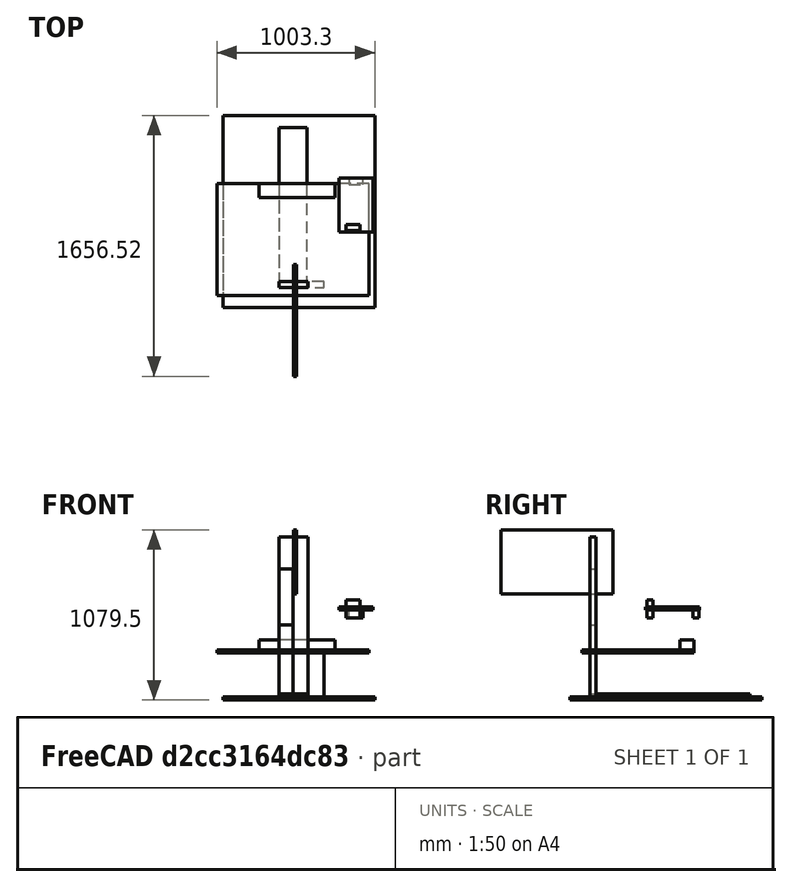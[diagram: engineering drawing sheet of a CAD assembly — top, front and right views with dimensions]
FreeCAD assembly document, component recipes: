
FREECAD ASSEMBLY — COMPONENT RECIPES ("flightDeck-rough")

This assembly document has 22 components, labeled P0..P21 below (a component is one placed body or linked part). 22 of them carry a construction recipe — the FreeCAD feature program that regenerates the part from scratch, quoted from this document or its linked companion documents; the rest are supplied as boundary geometry only. No exploded tour is included for this assembly.
COMPONENT P0 — recipe-attached ("panel-chairDeck", modeled in this document).
Construction recipe (the document's own serialized feature program — sketch geometry with constraints, then the solid features built on it; lengths are millimeters unless a unit is written):

FEATURE [Sketcher::SketchObject] Sketch013
  ArcFitTolerance = 1e-06
  AttachmentSupport = -> [XY_Plane007]
  ExternalBSplineMaxDegree = 5
  ExternalBSplineTolerance = 0.0001
  FixShape = 1
  FullyConstrained = true
  InternalTolerance = 1e-06
  InvalidShape = false
  MakeInternals = false
  MapMode = 5
  Support = -> [XY_Plane007]
  TreeRank = 114
  ValidateShape = false
  sketch-geometry (4):
    g0: LineSegment StartX=0 StartY=0 StartZ=0 EndX=965.2 EndY=0 EndZ=0
    g1: LineSegment StartX=965.2 StartY=0 StartZ=0 EndX=965.2 EndY=711.2 EndZ=0
    g2: LineSegment StartX=965.2 StartY=711.2 StartZ=0 EndX=0 EndY=711.2 EndZ=0
    g3: LineSegment StartX=0 StartY=711.2 StartZ=0 EndX=0 EndY=0 EndZ=0
  constraints (11):
    c: Coincident(g0,g1)
    c: Coincident(g1,g2)
    c: Coincident(g2,g3)
    c: Coincident(g3,g0)
    c: Horizontal(g0)
    c: Horizontal(g2)
    c: Vertical(g1)
    c: Vertical(g3)
    c: Coincident(g0,g-1)
    c: DistanceX(g0,g0) = 965.2
    c: DistanceY(g3,g3) = 711.2
FEATURE [PartDesign::Pad] Pad001
  AddSubType = 0
  AlongSketchNormal = false
  AutoTaperInnerAngle = true
  CheckUpToFaceLimits = true
  ClaimChildren = false
  Direction = (0,0,1)
  Fit = 0
  FitJoin = 0
  FixShape = 1
  InnerFit = 0
  InnerFitJoin = 0
  InvalidShape = false
  Length = 19.05
  Length2 = 100
  Linearize = true
  NewSolid = false
  Profile = -> Sketch013
  Refine = true
  Suppress = false
  TaperInnerAngle = 0
  TaperInnerAngleRev = 0
  TreeRank = 115
  Type = 0
  ValidateShape = false
  _ProfileBasedVersion = 1
FEATURE [PartDesign::Body] Body007  label="panel-chairDeck"
  AutoGroupSolids = false
  ClaimAllChildren = false
  ExportMode = 0
  FixShape = 1
  Group = -> [Sketch013,Pad001]
  InvalidShape = false
  Origin = -> Origin007
  Placement = pos=(-393.7,-50.7998,279.4) rot=(0,0,1;0rad)
  Tip = -> Pad001
  TreeRank = 113
  ValidateShape = false
  _ExportChildren = -> [Pad001]
  _GroupVersion = 1
COMPONENT P1 — recipe-attached ("panel-chairFloor", modeled in this document).
Construction recipe (the document's own serialized feature program — sketch geometry with constraints, then the solid features built on it; lengths are millimeters unless a unit is written):

FEATURE [Sketcher::SketchObject] Sketch014
  ArcFitTolerance = 1e-06
  AttachmentSupport = -> [XY_Plane008]
  ExternalBSplineMaxDegree = 5
  ExternalBSplineTolerance = 0.0001
  FixShape = 1
  FullyConstrained = true
  InternalTolerance = 1e-06
  InvalidShape = false
  MakeInternals = false
  MapMode = 5
  Support = -> [XY_Plane008]
  TreeRank = 126
  ValidateShape = false
  sketch-geometry (4):
    g0: LineSegment StartX=0 StartY=0 StartZ=0 EndX=965.2 EndY=0 EndZ=0
    g1: LineSegment StartX=965.2 StartY=0 StartZ=0 EndX=965.2 EndY=1219.2 EndZ=0
    g2: LineSegment StartX=965.2 StartY=1219.2 StartZ=0 EndX=0 EndY=1219.2 EndZ=0
    g3: LineSegment StartX=0 StartY=1219.2 StartZ=0 EndX=0 EndY=0 EndZ=0
  constraints (11):
    c: Coincident(g0,g1)
    c: Coincident(g1,g2)
    c: Coincident(g2,g3)
    c: Coincident(g3,g0)
    c: Horizontal(g0)
    c: Horizontal(g2)
    c: Vertical(g1)
    c: Vertical(g3)
    c: Coincident(g0,g-1)
    c: DistanceX(g0,g0) = 965.2
    c: DistanceY(g3,g3) = 1219.2
FEATURE [PartDesign::Pad] Pad002
  AddSubType = 0
  AlongSketchNormal = false
  AutoTaperInnerAngle = true
  CheckUpToFaceLimits = true
  ClaimChildren = false
  Direction = (0,0,1)
  Fit = 0
  FitJoin = 0
  FixShape = 1
  InnerFit = 0
  InnerFitJoin = 0
  InvalidShape = false
  Length = 19.05
  Length2 = 100
  Linearize = true
  NewSolid = false
  Profile = -> Sketch014
  Refine = true
  Suppress = false
  TaperInnerAngle = 0
  TaperInnerAngleRev = 0
  TreeRank = 127
  Type = 0
  ValidateShape = false
  _ProfileBasedVersion = 1
FEATURE [PartDesign::Body] Body008  label="panel-chairFloor"
  AutoGroupSolids = false
  ClaimAllChildren = false
  ExportMode = 0
  FixShape = 1
  Group = -> [Sketch014,Pad002]
  InvalidShape = false
  Origin = -> Origin008
  Placement = pos=(-355.6,-127,-19.0502) rot=(0,0,1;0rad)
  Tip = -> Pad002
  TreeRank = 125
  ValidateShape = false
  _ExportChildren = -> [Pad002]
  _GroupVersion = 1
COMPONENT P2 — recipe-attached ("panel-pedalsDeck", modeled in this document).
Construction recipe (the document's own serialized feature program — sketch geometry with constraints, then the solid features built on it; lengths are millimeters unless a unit is written):

FEATURE [Sketcher::SketchObject] Sketch016
  ArcFitTolerance = 1e-06
  AttachmentSupport = -> [XY_Plane010]
  ExternalBSplineMaxDegree = 5
  ExternalBSplineTolerance = 0.0001
  FixShape = 1
  FullyConstrained = false
  InternalTolerance = 1e-06
  InvalidShape = false
  MakeInternals = false
  MapMode = 5
  Support = -> [XY_Plane010]
  TreeRank = 159
  ValidateShape = false
  sketch-geometry (4):
    g0: LineSegment StartX=-351.816 StartY=864.428 StartZ=0 EndX=359.384 EndY=864.428 EndZ=0
    g1: LineSegment StartX=359.384 StartY=864.428 StartZ=0 EndX=359.384 EndY=1270.83 EndZ=0
    g2: LineSegment StartX=359.384 StartY=1270.83 StartZ=0 EndX=-351.816 EndY=1270.83 EndZ=0
    g3: LineSegment StartX=-351.816 StartY=1270.83 StartZ=0 EndX=-351.816 EndY=864.428 EndZ=0
  constraints (10):
    c: Coincident(g0,g1)
    c: Coincident(g1,g2)
    c: Coincident(g2,g3)
    c: Coincident(g3,g0)
    c: Horizontal(g0)
    c: Horizontal(g2)
    c: Vertical(g1)
    c: Vertical(g3)
    c: DistanceX(g0,g0) = 711.2
    c: DistanceY(g1,g1) = 406.4
FEATURE [PartDesign::Pad] Pad004
  AddSubType = 0
  AlongSketchNormal = false
  AutoTaperInnerAngle = true
  CheckUpToFaceLimits = true
  ClaimChildren = false
  Direction = (0,0,1)
  Fit = 0
  FitJoin = 0
  FixShape = 1
  InnerFit = 0
  InnerFitJoin = 0
  InvalidShape = false
  Length = 19.05
  Length2 = 100
  Linearize = true
  NewSolid = false
  Profile = -> Sketch016
  Refine = true
  Suppress = false
  TaperInnerAngle = 0
  TaperInnerAngleRev = 0
  TreeRank = 160
  Type = 0
  ValidateShape = false
  _ProfileBasedVersion = 1
FEATURE [PartDesign::Body] Body010  label="panel-pedalsDeck"
  AutoGroupSolids = false
  ClaimAllChildren = false
  ExportMode = 0
  FixShape = 1
  Group = -> [Sketch016,Pad004]
  InvalidShape = false
  Origin = -> Origin010
  Placement = pos=(92.6838,-212.506,-210.378) rot=(0.57735,0.57735,0.57735;2.0944rad)
  Tip = -> Pad004
  TreeRank = 158
  ValidateShape = false
  _ExportChildren = -> [Pad004]
  _GroupVersion = 1
COMPONENT P3 — recipe-attached ("timber-tilt", modeled in this document).
Construction recipe (the document's own serialized feature program — sketch geometry with constraints, then the solid features built on it; lengths are millimeters unless a unit is written):

FEATURE [Sketcher::SketchObject] Sketch018
  ArcFitTolerance = 1e-06
  AttachmentSupport = -> [XY_Plane012]
  ExternalBSplineMaxDegree = 5
  ExternalBSplineTolerance = 0.0001
  FixShape = 1
  FullyConstrained = true
  InternalTolerance = 1e-06
  InvalidShape = false
  MakeInternals = false
  MapMode = 5
  Support = -> [XY_Plane012]
  TreeRank = 191
  ValidateShape = false
  sketch-geometry (4):
    g0: LineSegment StartX=0 StartY=0 StartZ=0 EndX=88.9 EndY=0 EndZ=0
    g1: LineSegment StartX=88.9 StartY=0 StartZ=0 EndX=88.9 EndY=63.5 EndZ=0
    g2: LineSegment StartX=88.9 StartY=63.5 StartZ=0 EndX=0 EndY=63.5 EndZ=0
    g3: LineSegment StartX=0 StartY=63.5 StartZ=0 EndX=0 EndY=0 EndZ=0
  constraints (11):
    c: Coincident(g0,g1)
    c: Coincident(g1,g2)
    c: Coincident(g2,g3)
    c: Coincident(g3,g0)
    c: Horizontal(g0)
    c: Horizontal(g2)
    c: Vertical(g1)
    c: Vertical(g3)
    c: Coincident(g0,g-1)
    c: DistanceX(g0,g0) = 88.9
    c: DistanceY(g3,g3) = 63.5
FEATURE [PartDesign::Pad] Pad006
  AddSubType = 0
  AlongSketchNormal = false
  AutoTaperInnerAngle = true
  CheckUpToFaceLimits = true
  ClaimChildren = false
  Direction = (0,0,1)
  Fit = 0
  FitJoin = 0
  FixShape = 1
  InnerFit = 0
  InnerFitJoin = 0
  InvalidShape = false
  Length = 482.6
  Length2 = 100
  Linearize = true
  NewSolid = false
  Profile = -> Sketch018
  Refine = true
  Suppress = false
  TaperInnerAngle = 0
  TaperInnerAngleRev = 0
  TreeRank = 192
  Type = 0
  ValidateShape = false
  _ProfileBasedVersion = 1
FEATURE [PartDesign::Body] Body012  label="timber-tilt"
  AutoGroupSolids = false
  ClaimAllChildren = false
  ExportMode = 0
  FixShape = 1
  Group = -> [Sketch018,Pad006]
  InvalidShape = false
  Origin = -> Origin012
  Placement = pos=(355.6,660.4,298.45) rot=(0.57735,-0.57735,-0.57735;2.0944rad)
  Tip = -> Pad006
  TreeRank = 190
  ValidateShape = false
  _ExportChildren = -> [Pad006]
  _GroupVersion = 1
COMPONENT P4 — recipe-attached ("timber-sideStick", modeled in this document).
Construction recipe (the document's own serialized feature program — sketch geometry with constraints, then the solid features built on it; lengths are millimeters unless a unit is written):

FEATURE [Sketcher::SketchObject] Sketch022
  ArcFitTolerance = 1e-06
  AttachmentSupport = -> [XY_Plane016]
  ExternalBSplineMaxDegree = 5
  ExternalBSplineTolerance = 0.0001
  FixShape = 1
  FullyConstrained = true
  InternalTolerance = 1e-06
  InvalidShape = false
  MakeInternals = false
  MapMode = 5
  Support = -> [XY_Plane016]
  TreeRank = 244
  ValidateShape = false
  sketch-geometry (4):
    g0: LineSegment StartX=0 StartY=0 StartZ=0 EndX=88.9 EndY=0 EndZ=0
    g1: LineSegment StartX=88.9 StartY=0 StartZ=0 EndX=88.9 EndY=38.1 EndZ=0
    g2: LineSegment StartX=88.9 StartY=38.1 StartZ=0 EndX=0 EndY=38.1 EndZ=0
    g3: LineSegment StartX=0 StartY=38.1 StartZ=0 EndX=0 EndY=0 EndZ=0
  constraints (11):
    c: Coincident(g0,g1)
    c: Coincident(g1,g2)
    c: Coincident(g2,g3)
    c: Coincident(g3,g0)
    c: Horizontal(g0)
    c: Horizontal(g2)
    c: Vertical(g1)
    c: Vertical(g3)
    c: Coincident(g0,g-1)
    c: DistanceY(g3,g3) = 38.1
    c: DistanceX(g0,g0) = 88.9
FEATURE [PartDesign::Pad] Pad010
  AddSubType = 0
  AlongSketchNormal = false
  AutoTaperInnerAngle = true
  CheckUpToFaceLimits = true
  ClaimChildren = false
  Direction = (0,0,1)
  Fit = 0
  FitJoin = 0
  FixShape = 1
  InnerFit = 0
  InnerFitJoin = 0
  InvalidShape = false
  Length = 114.3
  Length2 = 100
  Linearize = true
  NewSolid = false
  Profile = -> Sketch022
  Refine = true
  Suppress = false
  TaperInnerAngle = 0
  TaperInnerAngleRev = 0
  TreeRank = 245
  Type = 0
  ValidateShape = false
  _ProfileBasedVersion = 1
FEATURE [PartDesign::Body] Body016  label="timber-sideStick"
  AutoGroupSolids = false
  ClaimAllChildren = false
  ExportMode = 0
  FixShape = 1
  Group = -> [Sketch022,Pad010]
  InvalidShape = false
  Origin = -> Origin016
  Placement = pos=(425.45,361.95,501.65) rot=(0,0,1;0rad)
  Tip = -> Pad010
  TreeRank = 247
  ValidateShape = false
  _ExportChildren = -> [Pad010]
  _GroupVersion = 1
COMPONENT P5 — recipe-attached ("timber-sideStick-front", modeled in this document).
Construction recipe (the document's own serialized feature program — sketch geometry with constraints, then the solid features built on it; lengths are millimeters unless a unit is written):

FEATURE [Sketcher::SketchObject] Sketch023
  ArcFitTolerance = 1e-06
  AttachmentSupport = -> [XY_Plane017]
  ExternalBSplineMaxDegree = 5
  ExternalBSplineTolerance = 0.0001
  FixShape = 1
  FullyConstrained = true
  InternalTolerance = 1e-06
  InvalidShape = false
  MakeInternals = false
  MapMode = 5
  Support = -> [XY_Plane017]
  TreeRank = 259
  ValidateShape = false
  sketch-geometry (4):
    g0: LineSegment StartX=0 StartY=0 StartZ=0 EndX=88.9 EndY=0 EndZ=0
    g1: LineSegment StartX=88.9 StartY=0 StartZ=0 EndX=88.9 EndY=38.1 EndZ=0
    g2: LineSegment StartX=88.9 StartY=38.1 StartZ=0 EndX=0 EndY=38.1 EndZ=0
    g3: LineSegment StartX=0 StartY=38.1 StartZ=0 EndX=0 EndY=0 EndZ=0
  constraints (11):
    c: Coincident(g0,g1)
    c: Coincident(g1,g2)
    c: Coincident(g2,g3)
    c: Coincident(g3,g0)
    c: Horizontal(g0)
    c: Horizontal(g2)
    c: Vertical(g1)
    c: Vertical(g3)
    c: Coincident(g0,g-1)
    c: DistanceY(g3,g3) = 38.1
    c: DistanceX(g0,g0) = 88.9
FEATURE [PartDesign::Pad] Pad011
  AddSubType = 0
  AlongSketchNormal = false
  AutoTaperInnerAngle = true
  CheckUpToFaceLimits = true
  ClaimChildren = false
  Direction = (0,0,1)
  Fit = 0
  FitJoin = 0
  FixShape = 1
  InnerFit = 0
  InnerFitJoin = 0
  InvalidShape = false
  Length = 69.85
  Length2 = 100
  Linearize = true
  NewSolid = false
  Profile = -> Sketch023
  Refine = true
  Suppress = false
  TaperInnerAngle = 0
  TaperInnerAngleRev = 0
  TreeRank = 260
  Type = 0
  ValidateShape = false
  _ProfileBasedVersion = 1
FEATURE [PartDesign::Body] Body017  label="timber-sideStick-front"
  AutoGroupSolids = false
  ClaimAllChildren = false
  ExportMode = 0
  FixShape = 1
  Group = -> [Sketch023,Pad011]
  InvalidShape = false
  Origin = -> Origin017
  Placement = pos=(444.5,654.05,501.65) rot=(0,0,1;0rad)
  Tip = -> Pad011
  TreeRank = 258
  ValidateShape = false
  _ExportChildren = -> [Pad011]
  _GroupVersion = 1
COMPONENT P6 — recipe-attached ("Link(timber-floorToChair)", modeled in this document).
Construction recipe (the document's own serialized feature program — sketch geometry with constraints, then the solid features built on it; lengths are millimeters unless a unit is written):

FEATURE [Sketcher::SketchObject] Sketch012
  ArcFitTolerance = 1e-06
  AttachmentSupport = -> [XY_Plane006]
  ExternalBSplineMaxDegree = 5
  ExternalBSplineTolerance = 0.0001
  FixShape = 1
  FullyConstrained = true
  InternalTolerance = 1e-06
  InvalidShape = false
  MakeInternals = false
  MapMode = 5
  Support = -> [XY_Plane006]
  TreeRank = 92
  ValidateShape = false
  sketch-geometry (4):
    g0: LineSegment StartX=0 StartY=0 StartZ=0 EndX=285.75 EndY=0 EndZ=0
    g1: LineSegment StartX=285.75 StartY=0 StartZ=0 EndX=285.75 EndY=38.1 EndZ=0
    g2: LineSegment StartX=285.75 StartY=38.1 StartZ=0 EndX=0 EndY=38.1 EndZ=0
    g3: LineSegment StartX=0 StartY=38.1 StartZ=0 EndX=0 EndY=0 EndZ=0
  constraints (11):
    c: Coincident(g0,g1)
    c: Coincident(g1,g2)
    c: Coincident(g2,g3)
    c: Coincident(g3,g0)
    c: Horizontal(g0)
    c: Horizontal(g2)
    c: Vertical(g1)
    c: Vertical(g3)
    c: Coincident(g0,g-1)
    c: DistanceX(g0,g0) = 285.75
    c: DistanceY(g3,g3) = 38.1
FEATURE [PartDesign::Pad] Pad
  AddSubType = 0
  AlongSketchNormal = false
  AutoTaperInnerAngle = true
  CheckUpToFaceLimits = true
  ClaimChildren = false
  Direction = (0,0,1)
  Fit = 0
  FitJoin = 0
  FixShape = 1
  InnerFit = 0
  InnerFitJoin = 0
  InvalidShape = false
  Length = 279.4
  Length2 = 100
  Linearize = true
  NewSolid = false
  Profile = -> Sketch012
  Refine = true
  Suppress = false
  TaperInnerAngle = 0
  TaperInnerAngleRev = 0
  TreeRank = 93
  Type = 0
  ValidateShape = false
  _ProfileBasedVersion = 1
FEATURE [PartDesign::Body] Body006  label="timber-floorToChair"
  AutoGroupSolids = false
  ClaimAllChildren = false
  ExportMode = 0
  FixShape = 1
  Group = -> [Sketch012,Pad]
  InvalidShape = false
  Origin = -> Origin006
  Tip = -> Pad
  TreeRank = 94
  ValidateShape = false
  _ExportChildren = -> [Pad]
  _GroupVersion = 1
COMPONENT P7 — same part as P6; its construction recipe is shown at P6.
COMPONENT P8 — same part as P6; its construction recipe is shown at P6.
COMPONENT P9 — same part as P6; its construction recipe is shown at P6.
COMPONENT P10 — same part as P6; its construction recipe is shown at P6.
COMPONENT P11 — same part as P6; its construction recipe is shown at P6.
COMPONENT P12 — recipe-attached ("Link006(timber-floorToPedals)", modeled in this document).
Construction recipe (the document's own serialized feature program — sketch geometry with constraints, then the solid features built on it; lengths are millimeters unless a unit is written):

FEATURE [Sketcher::SketchObject] Sketch015
  ArcFitTolerance = 1e-06
  AttachmentSupport = -> [XY_Plane009]
  ExternalBSplineMaxDegree = 5
  ExternalBSplineTolerance = 0.0001
  FixShape = 1
  FullyConstrained = true
  InternalTolerance = 1e-06
  InvalidShape = false
  MakeInternals = false
  MapMode = 5
  Support = -> [XY_Plane009]
  TreeRank = 141
  ValidateShape = false
  sketch-geometry (4):
    g0: LineSegment StartX=0 StartY=0 StartZ=0 EndX=88.9 EndY=0 EndZ=0
    g1: LineSegment StartX=88.9 StartY=0 StartZ=0 EndX=88.9 EndY=38.1 EndZ=0
    g2: LineSegment StartX=88.9 StartY=38.1 StartZ=0 EndX=0 EndY=38.1 EndZ=0
    g3: LineSegment StartX=0 StartY=38.1 StartZ=0 EndX=0 EndY=0 EndZ=0
  constraints (11):
    c: Coincident(g0,g1)
    c: Coincident(g1,g2)
    c: Coincident(g2,g3)
    c: Coincident(g3,g0)
    c: Horizontal(g0)
    c: Horizontal(g2)
    c: Vertical(g1)
    c: Vertical(g3)
    c: Coincident(g0,g-1)
    c: DistanceY(g3,g3) = 38.1
    c: DistanceX(g0,g0) = 88.9
FEATURE [PartDesign::Pad] Pad003
  AddSubType = 0
  AlongSketchNormal = false
  AutoTaperInnerAngle = true
  CheckUpToFaceLimits = true
  ClaimChildren = false
  Direction = (0,0,1)
  Fit = 0
  FitJoin = 0
  FixShape = 1
  InnerFit = 0
  InnerFitJoin = 0
  InvalidShape = false
  Length = 812.8
  Length2 = 100
  Linearize = true
  NewSolid = false
  Profile = -> Sketch015
  Refine = true
  Suppress = false
  TaperInnerAngle = 0
  TaperInnerAngleRev = 0
  TreeRank = 142
  Type = 0
  ValidateShape = false
  _ProfileBasedVersion = 1
FEATURE [PartDesign::Body] Body009  label="timber-floorToPedals"
  AutoGroupSolids = false
  ClaimAllChildren = false
  ExportMode = 0
  FixShape = 1
  Group = -> [Sketch015,Pad003]
  InvalidShape = false
  Origin = -> Origin009
  Tip = -> Pad003
  TreeRank = 147
  ValidateShape = false
  _ExportChildren = -> [Pad003]
  _GroupVersion = 1
COMPONENT P13 — same part as P12; its construction recipe is shown at P12.
COMPONENT P14 — recipe-attached ("Link008(timber-floorToWheel)", modeled in this document).
Construction recipe (the document's own serialized feature program — sketch geometry with constraints, then the solid features built on it; lengths are millimeters unless a unit is written):

FEATURE [Sketcher::SketchObject] Sketch017
  ArcFitTolerance = 1e-06
  AttachmentSupport = -> [XY_Plane011]
  ExternalBSplineMaxDegree = 5
  ExternalBSplineTolerance = 0.0001
  FixShape = 1
  FullyConstrained = true
  InternalTolerance = 1e-06
  InvalidShape = false
  MakeInternals = false
  MapMode = 5
  Support = -> [XY_Plane011]
  TreeRank = 172
  ValidateShape = false
  sketch-geometry (4):
    g0: LineSegment StartX=0 StartY=0 StartZ=0 EndX=88.9 EndY=0 EndZ=0
    g1: LineSegment StartX=88.9 StartY=0 StartZ=0 EndX=88.9 EndY=38.1 EndZ=0
    g2: LineSegment StartX=88.9 StartY=38.1 StartZ=0 EndX=0 EndY=38.1 EndZ=0
    g3: LineSegment StartX=0 StartY=38.1 StartZ=0 EndX=0 EndY=0 EndZ=0
  constraints (11):
    c: Coincident(g0,g1)
    c: Coincident(g1,g2)
    c: Coincident(g2,g3)
    c: Coincident(g3,g0)
    c: Horizontal(g0)
    c: Horizontal(g2)
    c: Vertical(g1)
    c: Vertical(g3)
    c: Coincident(g0,g-1)
    c: DistanceY(g3,g3) = 38.1
    c: DistanceX(g0,g0) = 88.9
FEATURE [PartDesign::Pad] Pad005
  AddSubType = 0
  AlongSketchNormal = false
  AutoTaperInnerAngle = true
  CheckUpToFaceLimits = true
  ClaimChildren = false
  Direction = (0,0,1)
  Fit = 0
  FitJoin = 0
  FixShape = 1
  InnerFit = 0
  InnerFitJoin = 0
  InvalidShape = false
  Length = 457.2
  Length2 = 100
  Linearize = true
  NewSolid = false
  Profile = -> Sketch017
  Refine = true
  Suppress = false
  TaperInnerAngle = 0
  TaperInnerAngleRev = 0
  TreeRank = 173
  Type = 0
  ValidateShape = false
  _ProfileBasedVersion = 1
FEATURE [PartDesign::Body] Body011  label="timber-floorToWheel"
  AutoGroupSolids = false
  ClaimAllChildren = false
  ExportMode = 0
  FixShape = 1
  Group = -> [Sketch017,Pad005]
  InvalidShape = false
  Origin = -> Origin011
  Tip = -> Pad005
  TreeRank = 171
  ValidateShape = false
  _ExportChildren = -> [Pad005]
  _GroupVersion = 1
COMPONENT P15 — same part as P14; its construction recipe is shown at P14.
COMPONENT P16 — same part as P14; its construction recipe is shown at P14.
COMPONENT P17 — recipe-attached ("Link011(timber-controlsDeck)", modeled in this document).
Construction recipe (the document's own serialized feature program — sketch geometry with constraints, then the solid features built on it; lengths are millimeters unless a unit is written):

FEATURE [Sketcher::SketchObject] Sketch019
  ArcFitTolerance = 1e-06
  AttachmentSupport = -> [XY_Plane013]
  ExternalBSplineMaxDegree = 5
  ExternalBSplineTolerance = 0.0001
  FixShape = 1
  FullyConstrained = true
  InternalTolerance = 1e-06
  InvalidShape = false
  MakeInternals = false
  MapMode = 5
  Support = -> [XY_Plane013]
  TreeRank = 203
  ValidateShape = false
  sketch-geometry (4):
    g0: LineSegment StartX=0 StartY=0 StartZ=0 EndX=184.15 EndY=0 EndZ=0
    g1: LineSegment StartX=184.15 StartY=0 StartZ=0 EndX=184.15 EndY=38.1 EndZ=0
    g2: LineSegment StartX=184.15 StartY=38.1 StartZ=0 EndX=0 EndY=38.1 EndZ=0
    g3: LineSegment StartX=0 StartY=38.1 StartZ=0 EndX=0 EndY=0 EndZ=0
  constraints (11):
    c: Coincident(g0,g1)
    c: Coincident(g1,g2)
    c: Coincident(g2,g3)
    c: Coincident(g3,g0)
    c: Horizontal(g0)
    c: Horizontal(g2)
    c: Vertical(g1)
    c: Vertical(g3)
    c: Coincident(g0,g-1)
    c: DistanceY(g3,g3) = 38.1
    c: DistanceX(g0,g0) = 184.15
FEATURE [PartDesign::Pad] Pad007
  AddSubType = 0
  AlongSketchNormal = false
  AutoTaperInnerAngle = true
  CheckUpToFaceLimits = true
  ClaimChildren = false
  Direction = (0,0,1)
  Fit = 0
  FitJoin = 0
  FixShape = 1
  InnerFit = 0
  InnerFitJoin = 0
  InvalidShape = false
  Length = 1016
  Length2 = 100
  Linearize = true
  NewSolid = false
  Profile = -> Sketch019
  Refine = true
  Suppress = false
  TaperInnerAngle = 0
  TaperInnerAngleRev = 0
  TreeRank = 204
  Type = 0
  ValidateShape = false
  _ProfileBasedVersion = 1
FEATURE [PartDesign::Body] Body013  label="timber-controlsDeck"
  AutoGroupSolids = false
  ClaimAllChildren = false
  ExportMode = 0
  FixShape = 1
  Group = -> [Sketch019,Pad007]
  InvalidShape = false
  Origin = -> Origin013
  Tip = -> Pad007
  TreeRank = 202
  ValidateShape = false
  _ExportChildren = -> [Pad007]
  _GroupVersion = 1
COMPONENT P18 — same part as P17; its construction recipe is shown at P17.
COMPONENT P19 — recipe-attached ("Link013(panel-controlsDeck)", modeled in this document).
Construction recipe (the document's own serialized feature program — sketch geometry with constraints, then the solid features built on it; lengths are millimeters unless a unit is written):

FEATURE [Sketcher::SketchObject] Sketch020
  ArcFitTolerance = 1e-06
  AttachmentSupport = -> [XY_Plane014]
  ExternalBSplineMaxDegree = 5
  ExternalBSplineTolerance = 0.0001
  FixShape = 1
  FullyConstrained = true
  InternalTolerance = 1e-06
  InvalidShape = false
  MakeInternals = false
  MapMode = 5
  Support = -> [XY_Plane014]
  TreeRank = 217
  ValidateShape = false
  sketch-geometry (4):
    g0: LineSegment StartX=0 StartY=0 StartZ=0 EndX=177.8 EndY=0 EndZ=0
    g1: LineSegment StartX=177.8 StartY=0 StartZ=0 EndX=177.8 EndY=1016 EndZ=0
    g2: LineSegment StartX=177.8 StartY=1016 StartZ=0 EndX=0 EndY=1016 EndZ=0
    g3: LineSegment StartX=0 StartY=1016 StartZ=0 EndX=0 EndY=0 EndZ=0
  constraints (11):
    c: Coincident(g0,g1)
    c: Coincident(g1,g2)
    c: Coincident(g2,g3)
    c: Coincident(g3,g0)
    c: Horizontal(g0)
    c: Horizontal(g2)
    c: Vertical(g1)
    c: Vertical(g3)
    c: Coincident(g0,g-1)
    c: DistanceX(g0,g0) = 177.8
    c: DistanceY(g3,g3) = 1016
FEATURE [PartDesign::Pad] Pad008
  AddSubType = 0
  AlongSketchNormal = false
  AutoTaperInnerAngle = true
  CheckUpToFaceLimits = true
  ClaimChildren = false
  Direction = (0,0,1)
  Fit = 0
  FitJoin = 0
  FixShape = 1
  InnerFit = 0
  InnerFitJoin = 0
  InvalidShape = false
  Length = 19.05
  Length2 = 100
  Linearize = true
  NewSolid = false
  Profile = -> Sketch020
  Refine = true
  Suppress = false
  TaperInnerAngle = 0
  TaperInnerAngleRev = 0
  TreeRank = 218
  Type = 0
  ValidateShape = false
  _ProfileBasedVersion = 1
FEATURE [PartDesign::Body] Body014  label="panel-controlsDeck"
  AutoGroupSolids = false
  ClaimAllChildren = false
  ExportMode = 0
  FixShape = 1
  Group = -> [Sketch020,Pad008]
  InvalidShape = false
  Origin = -> Origin014
  Tip = -> Pad008
  TreeRank = 216
  ValidateShape = false
  _ExportChildren = -> [Pad008]
  _GroupVersion = 1
COMPONENT P20 — same part as P19; its construction recipe is shown at P19.
COMPONENT P21 — recipe-attached ("Link015(panel-sidestick)", modeled in this document).
Construction recipe (the document's own serialized feature program — sketch geometry with constraints, then the solid features built on it; lengths are millimeters unless a unit is written):

FEATURE [Sketcher::SketchObject] Sketch021
  ArcFitTolerance = 1e-06
  AttachmentSupport = -> [XY_Plane015]
  ExternalBSplineMaxDegree = 5
  ExternalBSplineTolerance = 0.0001
  FixShape = 1
  FullyConstrained = true
  InternalTolerance = 1e-06
  InvalidShape = false
  MakeInternals = false
  MapMode = 5
  Support = -> [XY_Plane015]
  TreeRank = 231
  ValidateShape = false
  sketch-geometry (4):
    g0: LineSegment StartX=0 StartY=0 StartZ=0 EndX=215.9 EndY=0 EndZ=0
    g1: LineSegment StartX=215.9 StartY=0 StartZ=0 EndX=215.9 EndY=342.9 EndZ=0
    g2: LineSegment StartX=215.9 StartY=342.9 StartZ=0 EndX=0 EndY=342.9 EndZ=0
    g3: LineSegment StartX=0 StartY=342.9 StartZ=0 EndX=0 EndY=0 EndZ=0
  constraints (11):
    c: Coincident(g0,g1)
    c: Coincident(g1,g2)
    c: Coincident(g2,g3)
    c: Coincident(g3,g0)
    c: Horizontal(g0)
    c: Horizontal(g2)
    c: Vertical(g1)
    c: Vertical(g3)
    c: Coincident(g0,g-1)
    c: DistanceY(g3,g3) = 342.9
    c: DistanceX(g0,g0) = 215.9
FEATURE [PartDesign::Pad] Pad009
  AddSubType = 0
  AlongSketchNormal = false
  AutoTaperInnerAngle = true
  CheckUpToFaceLimits = true
  ClaimChildren = false
  Direction = (0,0,1)
  Fit = 0
  FitJoin = 0
  FixShape = 1
  InnerFit = 0
  InnerFitJoin = 0
  InvalidShape = false
  Length = 19.05
  Length2 = 100
  Linearize = true
  NewSolid = false
  Profile = -> Sketch021
  Refine = true
  Suppress = false
  TaperInnerAngle = 0
  TaperInnerAngleRev = 0
  TreeRank = 232
  Type = 0
  ValidateShape = false
  _ProfileBasedVersion = 1
FEATURE [PartDesign::Body] Body015  label="panel-sidestick"
  AutoGroupSolids = false
  ClaimAllChildren = false
  ExportMode = 0
  FixShape = 1
  Group = -> [Sketch021,Pad009]
  InvalidShape = false
  Origin = -> Origin015
  Placement = pos=(381,352.292,552.74) rot=(0,0,1;0rad)
  Tip = -> Pad009
  TreeRank = 248
  ValidateShape = false
  _ExportChildren = -> [Pad009]
  _GroupVersion = 1
PROVENANCE & LICENSES
A FreeCAD (.FCStd) document from a public repository crawl; recipes are the document's own serialized feature recipes (and, for linked parts, companion documents' recipes).
License: agpl-3.0.
